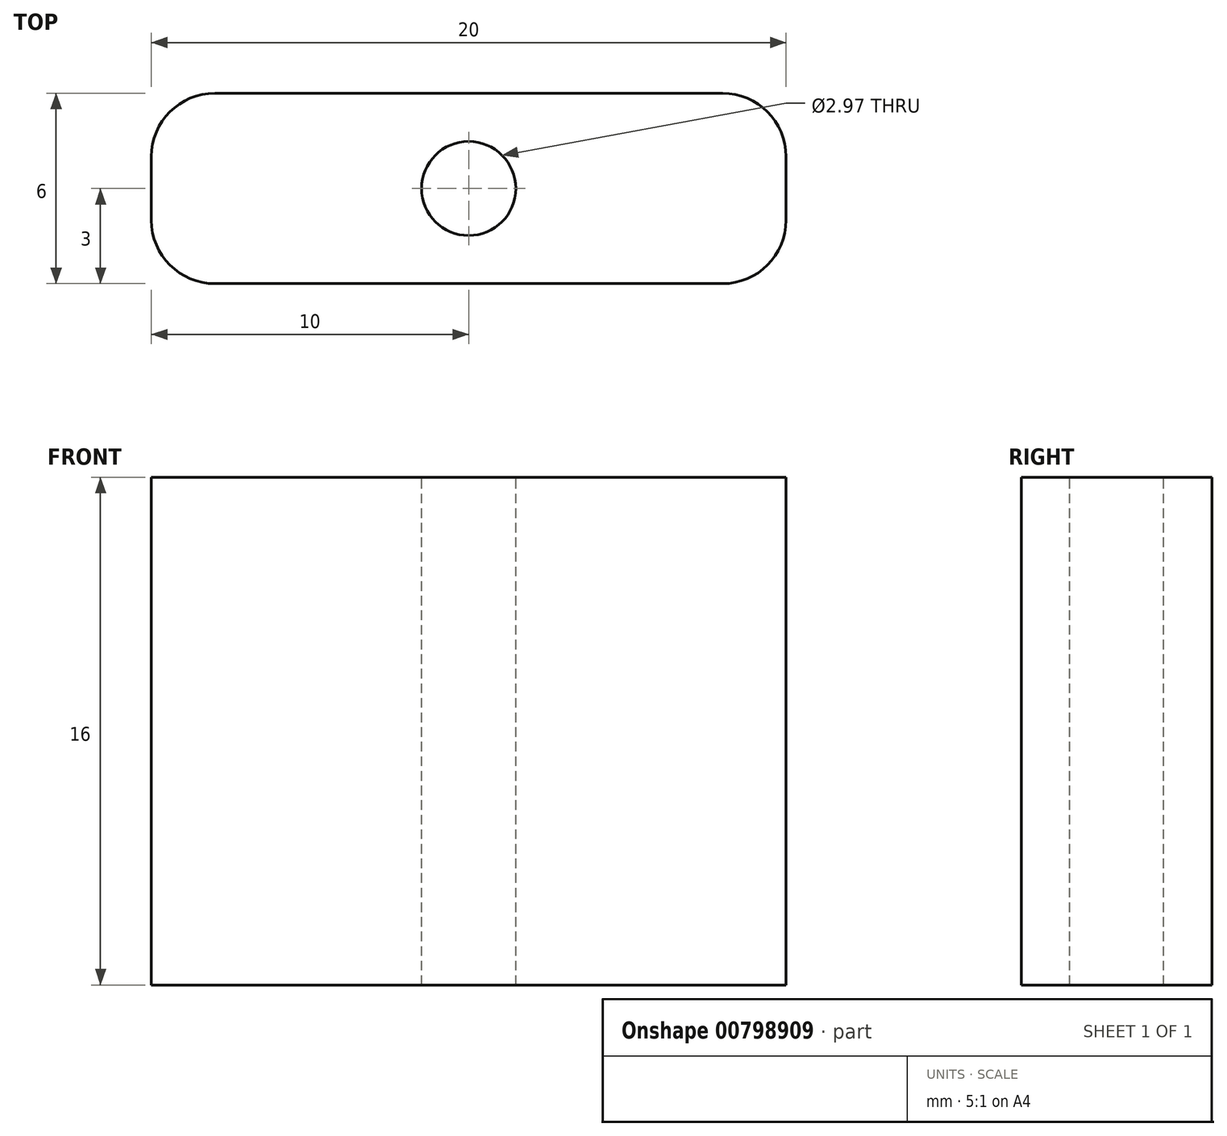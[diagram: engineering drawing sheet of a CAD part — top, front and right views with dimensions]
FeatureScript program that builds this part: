
annotation { "Feature Type Name" : "Feature", "Feature Type Description" : "" }
export const myFeature = defineFeature(function(context is Context, id is Id, definition is map)
    precondition{}
    {
        {
            var Q0;
            Q0=qCreatedBy(makeId("Top.planeOp"),FACE);
            var sketch = newSketch(context, id + "F0", { "sketchPlane" : qUnion([Q0])});
            skLineSegment(sketch, "E0.bottom", {"start": v(0, 0) * mm, "end": v(20, 0) * mm});
            skLineSegment(sketch, "E0.top", {"start": v(0, 6) * mm, "end": v(20, 6) * mm});
            skLineSegment(sketch, "E0.left", {"start": v(0, 0) * mm, "end": v(0, 6) * mm});
            skLineSegment(sketch, "E0.right", {"start": v(20, 0) * mm, "end": v(20, 6) * mm});
            skCircle(sketch, "E1", {"center": v(10, 3) * mm, "radius": 1.48 * mm});
            skPoint(sketch, "E1.centerSnap0", {"position": v(10, 6) * mm});
            skSolve(sketch);
        }
        {
            var Q0;
            Q0 = qSketchRegion(id + "F0", true);
            extrude(context, id + "F1", {"entities" : qUnion([Q0]), "oppositeDirection" : true, "depth" : 16 * mm, "offsetDistance" : 25 * mm});
        }
        {
            var Q0;
            Q0=makeQuery(id+"F1.opExtrude","SWEPT_EDGE",EDGE,{"disambiguationData":[OSD([sQuery(id+"F0.wireOp",EDGE,"E0.top"),sQuery(id+"F0.wireOp",EDGE,"E0.right")])]});
            var Q1;
            Q1=makeQuery(id+"F1.opExtrude","SWEPT_EDGE",EDGE,{"disambiguationData":[OSD([sQuery(id+"F0.wireOp",EDGE,"E0.top"),sQuery(id+"F0.wireOp",EDGE,"E0.left")])]});
            var Q2;
            Q2=makeQuery(id+"F1.opExtrude","SWEPT_EDGE",EDGE,{"disambiguationData":[OSD([sQuery(id+"F0.wireOp",EDGE,"E0.bottom"),sQuery(id+"F0.wireOp",EDGE,"E0.right")])]});
            var Q3;
            Q3=makeQuery(id+"F1.opExtrude","SWEPT_EDGE",EDGE,{"disambiguationData":[OSD([sQuery(id+"F0.wireOp",EDGE,"E0.bottom"),sQuery(id+"F0.wireOp",EDGE,"E0.left")])]});
            fillet(context, id + "F2", {"entities" : qUnion([Q0, Q1, Q2, Q3]), "radius" : 2 * mm, "tangentPropagation" : true, "allowEdgeOverflow" : false});
        }
    });
